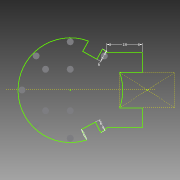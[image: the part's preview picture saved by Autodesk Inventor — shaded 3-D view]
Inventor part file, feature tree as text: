
AUTODESK INVENTOR PART (.ipt)
format: ipt  version: 2014 (Build 180170000, 170)  size: 143,872 bytes
history: native  units: mm
features: other x7, extrude x6
ambient origin geometry x8: Origin, YZ Plane, XZ Plane, XY Plane, X Axis, Y Axis, Z Axis, Center Point
bodies: Body1 (feature_tree)
feature tree (13):
  other  "Teller"
  other  "Dicke Stifte Außen"
  other  "Dünne Stifte Außen"
  other  "Dicke Stifte Vorn"
  other  "Dicke Stifte Hinten"
  other  "Dünne Stifte Vorn"
  other  "Dünne Stifte Hinten"
  extrude  "Extrusion13"  Depth=53.0mm
  extrude  "Extrusion14"  Depth=6.0mm
  extrude  "Extrusion15"  Depth=3.5mm
  extrude  "Extrusion16"  Depth=53.0mm
  extrude  "Extrusion17"  Depth=80.0mm TaperAngle=360.0deg
  extrude  "Extrusion18"  Depth=2.0mm
